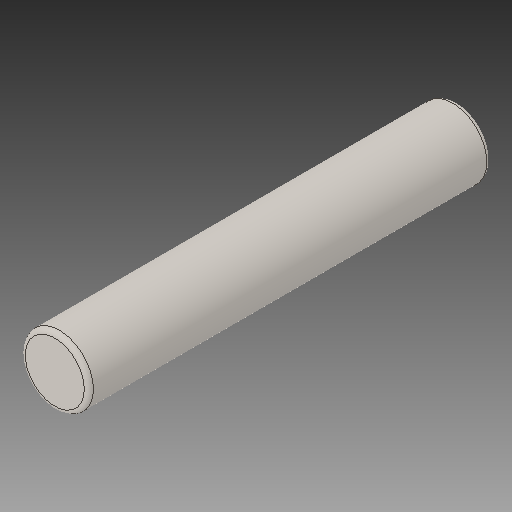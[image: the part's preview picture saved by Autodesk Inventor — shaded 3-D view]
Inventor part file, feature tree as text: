
AUTODESK INVENTOR PART (.ipt)
format: ipt  version: 2019.1 (Build 231200000, 200)  size: 98,816 bytes
history: mixed  units: in
note: dims shown in document units (in); Inventor stores cm internally (conversion verified against a paired STEP export)
features: fillet x1, imported_body x1
ambient origin geometry x8: Origin, YZ Plane, XZ Plane, XY Plane, X Axis, Y Axis, Z Axis, Center Point
bodies: Solid1 (imported_parasolid)
feature tree (2):
  fillet  "Fillet1"  [1 undecoded]
  imported_body  NMx_Import_Brep_tag  [imported B-rep: ~5 faces, bbox_mm=[0.2, 0.0, 17.7]]
note: 1 required parameter value undecoded (feature->parameter linkage not recoverable at this tier; creation-order binding heuristic only, values carry confidence <= 0.55)
